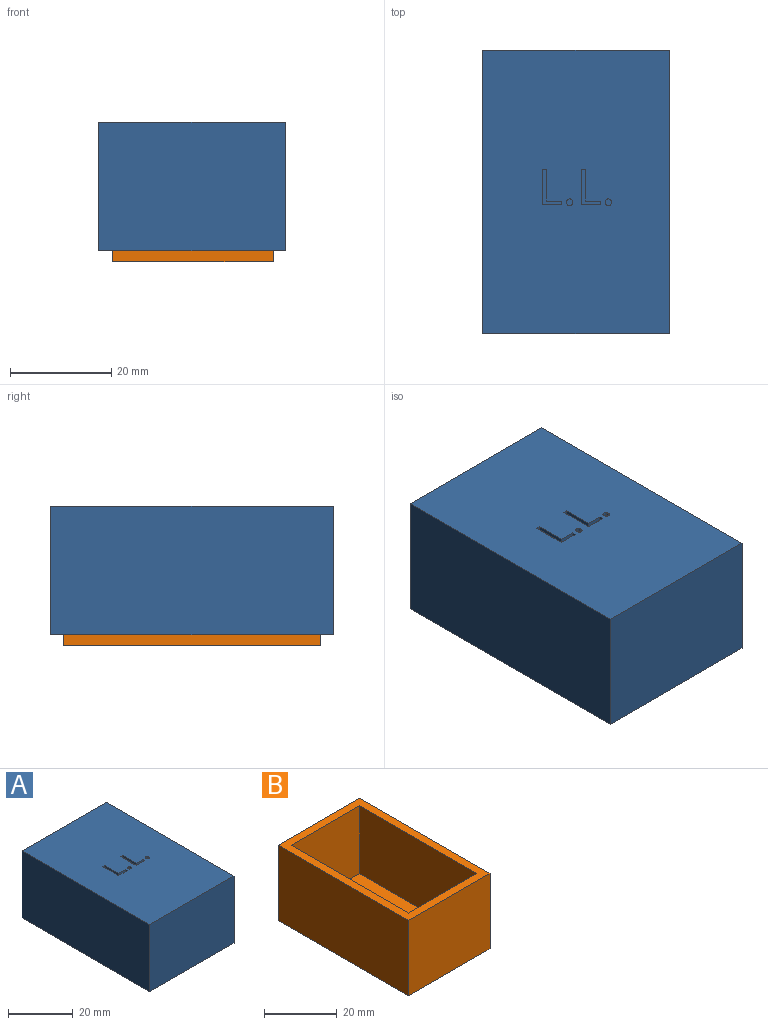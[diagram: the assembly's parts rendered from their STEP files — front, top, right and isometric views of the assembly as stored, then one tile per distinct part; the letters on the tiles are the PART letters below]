
ASSEMBLY  parts=2 mates=1
PART A: 43 faces, bbox 36.8x55.9x25.4 mm
  f0: plane 55.88x36.83mm, normal (0,0,1), area 2039.8mm2, adj f2,f3,f4,f5,f11,f12,f13,f14
  f1: plane 55.88x36.83mm, normal (0,0,-1), area 338.7mm2, adj f2,f3,f4,f5,f6,f7,f8,f9
  f2: plane 36.83x25.4mm, normal (0,1,0), area 935.5mm2, adj f0,f1,f3,f5
  f3: plane 55.88x25.4mm, normal (-1,0,0), area 1419.4mm2, adj f0,f1,f2,f4
  f4: plane 36.83x25.4mm, normal (0,-1,0), area 935.5mm2, adj f0,f1,f3,f5
  f5: plane 55.88x25.4mm, normal (1,0,0), area 1419.4mm2, adj f0,f1,f2,f4
  f6: plane 33.02x23.5mm, normal (0,-1,0), area 775.8mm2, adj f1,f7,f9,f10
  f7: plane 52.07x23.5mm, normal (1,0,0), area 1223.4mm2, adj f1,f6,f8,f10
  f8: plane 33.02x23.5mm, normal (0,1,0), area 775.8mm2, adj f1,f7,f9,f10
  f9: plane 52.07x23.5mm, normal (-1,0,0), area 1223.4mm2, adj f1,f6,f8,f10
  f10: plane 52.07x33.02mm, normal (0,0,-1), area 1719.4mm2, adj f6,f7,f8,f9
  f11: extruded ~0.76x0.48mm, area 0.4mm2, adj f0,f12,f18,f19
  f12: extruded ~0.76x0.49mm, area 0.4mm2, adj f0,f11,f13,f19
  f13: extruded ~0.76x0.4mm, area 0.3mm2, adj f0,f12,f14,f19
  f14: extruded ~0.76x0.43mm, area 0.4mm2, adj f0,f13,f15,f19
  f15: extruded ~0.76x0.48mm, area 0.4mm2, adj f0,f14,f16,f19
  f16: extruded ~0.76x0.48mm, area 0.4mm2, adj f0,f15,f17,f19
  f17: extruded ~0.76x0.43mm, area 0.4mm2, adj f0,f16,f18,f19
  f18: extruded ~0.76x0.42mm, area 0.4mm2, adj f0,f11,f17,f19
  f19: plane 1.29x1.15mm, normal (0,0,1), area 1.2mm2, adj f11,f12,f13,f14,f15,f16,f17,f18
  f20: plane 6.97x0.76mm, normal (1,0,0), area 5.3mm2, adj f0,f21,f25,f26
  f21: plane 3.89x0.76mm, normal (0,1,0), area 3mm2, adj f0,f20,f22,f26
  f22: plane 0.76x0.73mm, normal (-1,0,0), area 0.6mm2, adj f0,f21,f23,f26
  f23: plane 3.08x0.76mm, normal (0,-1,0), area 2.3mm2, adj f0,f22,f24,f26
  f24: plane 6.24x0.76mm, normal (-1,0,0), area 4.8mm2, adj f0,f23,f25,f26
  f25: plane 0.81x0.76mm, normal (0,-1,0), area 0.6mm2, adj f0,f20,f24,f26
  f26: plane 6.97x3.89mm, normal (0,0,1), area 7.9mm2, adj f20,f21,f22,f23,f24,f25
  f27: extruded ~0.76x0.48mm, area 0.4mm2, adj f0,f28,f34,f35
  f28: extruded ~0.76x0.49mm, area 0.4mm2, adj f0,f27,f29,f35
  f29: extruded ~0.76x0.4mm, area 0.3mm2, adj f0,f28,f30,f35
  f30: extruded ~0.76x0.43mm, area 0.4mm2, adj f0,f29,f31,f35
  f31: extruded ~0.76x0.48mm, area 0.4mm2, adj f0,f30,f32,f35
  f32: extruded ~0.76x0.48mm, area 0.4mm2, adj f0,f31,f33,f35
  f33: extruded ~0.76x0.43mm, area 0.4mm2, adj f0,f32,f34,f35
  f34: extruded ~0.76x0.42mm, area 0.4mm2, adj f0,f27,f33,f35
  f35: plane 1.29x1.15mm, normal (0,0,1), area 1.2mm2, adj f27,f28,f29,f30,f31,f32,f33,f34
  f36: plane 6.97x0.76mm, normal (1,0,0), area 5.3mm2, adj f0,f37,f41,f42
  f37: plane 3.89x0.76mm, normal (0,1,0), area 3mm2, adj f0,f36,f38,f42
  f38: plane 0.76x0.73mm, normal (-1,0,0), area 0.6mm2, adj f0,f37,f39,f42
  f39: plane 3.08x0.76mm, normal (0,-1,0), area 2.3mm2, adj f0,f38,f40,f42
  f40: plane 6.24x0.76mm, normal (-1,0,0), area 4.8mm2, adj f0,f39,f41,f42
  f41: plane 0.81x0.76mm, normal (0,-1,0), area 0.6mm2, adj f0,f36,f40,f42
  f42: plane 6.97x3.89mm, normal (0,0,1), area 7.9mm2, adj f36,f37,f38,f39,f40,f41
PART B: 11 faces, bbox 31.8x50.8x25.4 mm
  f0: plane 50.8x31.75mm, normal (0,0,1), area 393.5mm2, adj f1,f2,f3,f4,f6,f7,f8,f9
  f1: plane 31.75x25.4mm, normal (0,1,0), area 806.5mm2, adj f0,f2,f4,f5
  f2: plane 50.8x25.4mm, normal (-1,0,0), area 1290.3mm2, adj f0,f1,f3,f5
  f3: plane 31.75x25.4mm, normal (0,-1,0), area 806.5mm2, adj f0,f2,f4,f5
  f4: plane 50.8x25.4mm, normal (1,0,0), area 1290.3mm2, adj f0,f1,f3,f5
  f5: plane 50.8x31.75mm, normal (0,0,-1), area 1612.9mm2, adj f1,f2,f3,f4
  f6: plane 26.67x22.86mm, normal (0,-1,0), area 609.7mm2, adj f0,f7,f9,f10
  f7: plane 45.72x22.86mm, normal (1,0,0), area 1045.2mm2, adj f0,f6,f8,f10
  f8: plane 26.67x22.86mm, normal (0,1,0), area 609.7mm2, adj f0,f7,f9,f10
  f9: plane 45.72x22.86mm, normal (-1,0,0), area 1045.2mm2, adj f0,f6,f8,f10
  f10: plane 45.72x26.67mm, normal (0,0,1), area 1219.4mm2, adj f6,f7,f8,f9
PLACE A t=(-74.25,14.65,-89.99)mm
PLACE B t=(-36.87,12.75,-92.22)mm
MATE slider A.f9 <-> B.f9  axis (-1,0,0) through (-19.75,10.93,-78.25)mm
